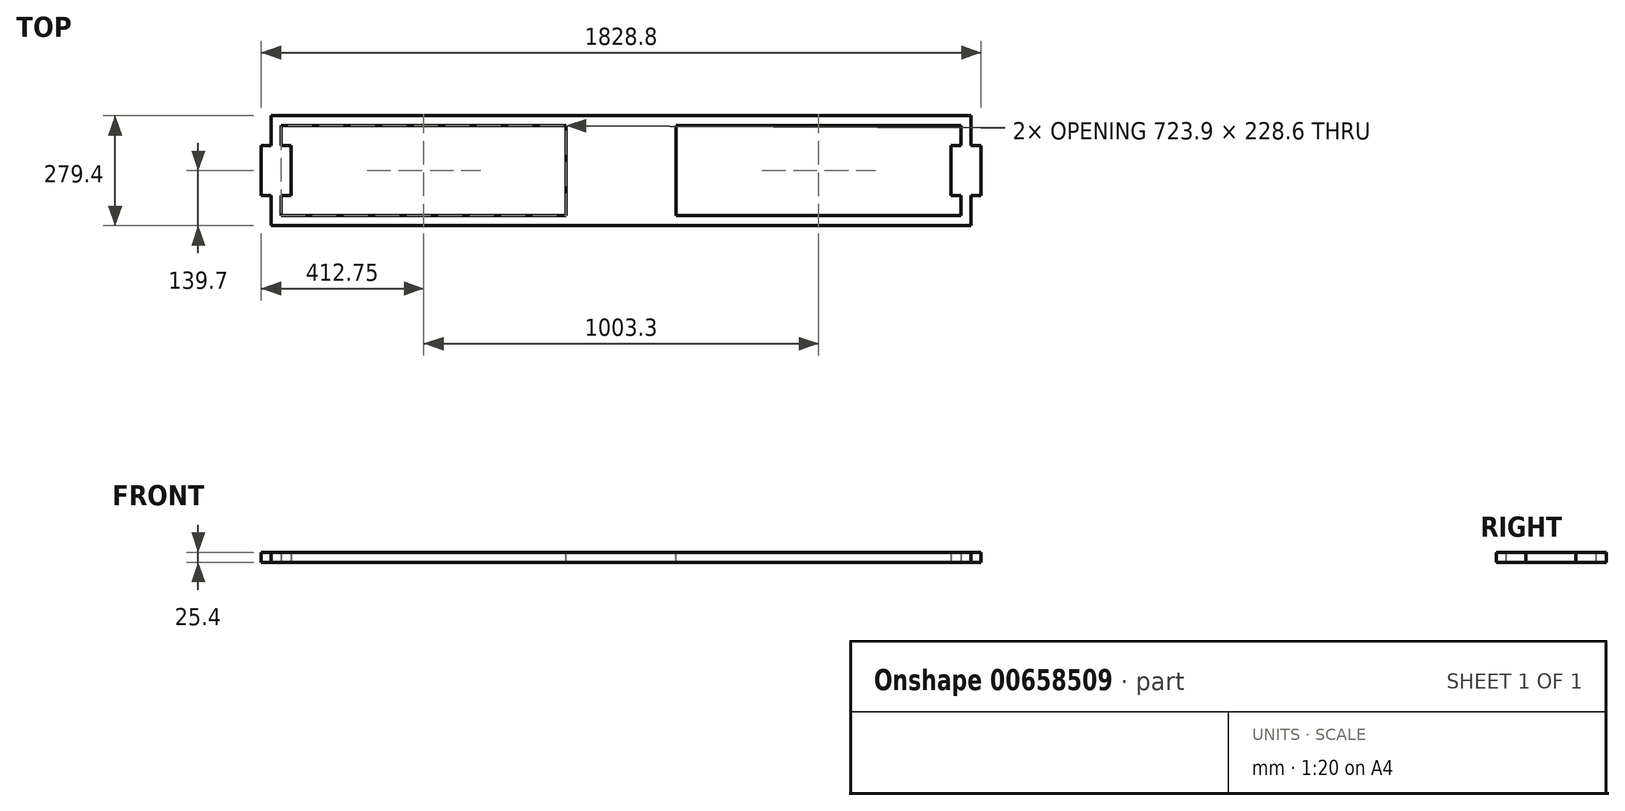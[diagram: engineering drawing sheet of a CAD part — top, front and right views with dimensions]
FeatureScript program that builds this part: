
annotation { "Feature Type Name" : "Feature", "Feature Type Description" : "" }
export const myFeature = defineFeature(function(context is Context, id is Id, definition is map)
    precondition{}
    {
        {
            var Q0;
            Q0=qCreatedBy(makeId("Top.planeOp"),FACE);
            var sketch = newSketch(context, id + "F0", { "sketchPlane" : qUnion([Q0])});
            skLineSegment(sketch, "E0.bottom", {"start": v(-889, 139.7) * mm, "end": v(889, 139.7) * mm});
            skLineSegment(sketch, "E0.top", {"start": v(-889, -139.7) * mm, "end": v(889, -139.7) * mm});
            skLineSegment(sketch, "E0.left", {"start": v(-889, 139.7) * mm, "end": v(-889, -139.7) * mm});
            skLineSegment(sketch, "E0.right", {"start": v(889, 139.7) * mm, "end": v(889, -139.7) * mm});
            skSolve(sketch);
        }
        {
            var Q0;
            Q0=makeQuery(id+"F0.imprint","IMPRINT",FACE,{"disambiguationData":[TD([[makeQuery(id+"F0.imprint","IMPRINT",EDGE,{"derivedFrom":sQuery(id+"F0.wireOp",EDGE,"E0.bottom")}),-1.0]])]});
            extrude(context, id + "F1", {"entities" : qUnion([Q0]), "depth" : 25.4 * mm, "offsetDistance" : 25.4 * mm});
        }
        {
            var Q0;
            Q0=makeQuery(id+"F1.opExtrude","CAP_FACE",FACE,{"disambiguationData":[OSD([sQuery(id+"F0.wireOp",EDGE,"E0.bottom"),sQuery(id+"F0.wireOp",EDGE,"E0.top"),sQuery(id+"F0.wireOp",EDGE,"E0.left"),sQuery(id+"F0.wireOp",EDGE,"E0.right")])],"isStart":false});
            var sketch = newSketch(context, id + "F2", { "sketchPlane" : qUnion([Q0])});
            skLineSegment(sketch, "E1.bottom", {"start": v(-863.6, 114.3) * mm, "end": v(863.6, 114.3) * mm});
            skLineSegment(sketch, "E1.top", {"start": v(-863.6, -114.3) * mm, "end": v(863.6, -114.3) * mm});
            skLineSegment(sketch, "E1.left", {"start": v(-863.6, 114.3) * mm, "end": v(-863.6, -114.3) * mm});
            skLineSegment(sketch, "E1.right", {"start": v(863.6, 114.3) * mm, "end": v(863.6, -114.3) * mm});
            skSolve(sketch);
        }
        {
            var Q0;
            Q0=makeQuery(id+"F2.imprint","IMPRINT",FACE,{"disambiguationData":[TD([[makeQuery(id+"F2.imprint","IMPRINT",EDGE,{"derivedFrom":sQuery(id+"F2.wireOp",EDGE,"E1.bottom")}),-1.0]])]});
            extrude(context, id + "F3", {"entities" : qUnion([Q0]), "operationType" : NewBodyOperationType.REMOVE, "endBound" : BoundingType.THROUGH_ALL, "oppositeDirection" : true, "depth" : 25.4 * mm, "offsetDistance" : 25.4 * mm});
        }
        {
            var Q0;
            Q0=qCreatedBy(makeId("Top.planeOp"),FACE);
            var sketch = newSketch(context, id + "F4", { "sketchPlane" : qUnion([Q0])});
            skLineSegment(sketch, "E2.bottom", {"start": v(-139.7, 139.7) * mm, "end": v(139.7, 139.7) * mm});
            skLineSegment(sketch, "E2.top", {"start": v(-139.7, -139.7) * mm, "end": v(139.7, -139.7) * mm});
            skLineSegment(sketch, "E2.left", {"start": v(-139.7, 139.7) * mm, "end": v(-139.7, -139.7) * mm});
            skLineSegment(sketch, "E2.right", {"start": v(139.7, 139.7) * mm, "end": v(139.7, -139.7) * mm});
            skSolve(sketch);
        }
        {
            var Q0;
            Q0=qSketchRegion(id+"F4",true);
            extrude(context, id + "F5", {"entities" : qUnion([Q0]), "operationType" : NewBodyOperationType.ADD, "depth" : 25.4 * mm, "offsetDistance" : 25.4 * mm});
        }
        {
            var Q0;
            Q0=makeQuery(id+"F1.opExtrude","SWEPT_FACE",FACE,{"disambiguationData":[OSD([sQuery(id+"F0.wireOp",EDGE,"E0.left")])]});
            var sketch = newSketch(context, id + "F6", { "sketchPlane" : qUnion([Q0])});
            skLineSegment(sketch, "E3.bottom", {"start": v(-63.5, 0) * mm, "end": v(63.5, 0) * mm});
            skLineSegment(sketch, "E3.top", {"start": v(-63.5, 25.4) * mm, "end": v(63.5, 25.4) * mm});
            skLineSegment(sketch, "E3.left", {"start": v(-63.5, 0) * mm, "end": v(-63.5, 25.4) * mm});
            skLineSegment(sketch, "E3.right", {"start": v(63.5, 0) * mm, "end": v(63.5, 25.4) * mm});
            skSolve(sketch);
        }
        {
            var Q0;
            Q0=makeQuery(id+"F6.imprint","IMPRINT",FACE,{"disambiguationData":[TD([[makeQuery(id+"F6.imprint","IMPRINT",EDGE,{"derivedFrom":sQuery(id+"F6.wireOp",EDGE,"E3.bottom")}),1.0]])]});
            extrude(context, id + "F7", {"entities" : qUnion([Q0]), "operationType" : NewBodyOperationType.ADD, "depth" : 25.4 * mm, "offsetDistance" : 25.4 * mm});
        }
        {
            var Q0;
            Q0=makeQuery(id+"F3.boolean.opBoolean","COPY",FACE,{"derivedFrom":makeQuery(id+"F3.opExtrude","SWEPT_FACE",FACE,{"disambiguationData":[OSD([sQuery(id+"F2.wireOp",EDGE,"E1.left")])]})});
            var sketch = newSketch(context, id + "F8", { "sketchPlane" : qUnion([Q0])});
            skLineSegment(sketch, "E4.bottom", {"start": v(-63.5, 25.4) * mm, "end": v(63.5, 25.4) * mm});
            skLineSegment(sketch, "E4.top", {"start": v(-63.5, 0) * mm, "end": v(63.5, 0) * mm});
            skLineSegment(sketch, "E4.left", {"start": v(-63.5, 25.4) * mm, "end": v(-63.5, 0) * mm});
            skLineSegment(sketch, "E4.right", {"start": v(63.5, 25.4) * mm, "end": v(63.5, 0) * mm});
            skSolve(sketch);
        }
        {
            var Q0;
            Q0=makeQuery(id+"F8.imprint","IMPRINT",FACE,{"disambiguationData":[TD([[makeQuery(id+"F8.imprint","IMPRINT",EDGE,{"derivedFrom":sQuery(id+"F8.wireOp",EDGE,"E4.bottom")}),1.0]])]});
            extrude(context, id + "F9", {"entities" : qUnion([Q0]), "operationType" : NewBodyOperationType.ADD, "depth" : 25.4 * mm, "offsetDistance" : 25.4 * mm});
        }
        {
            var Q0;
            Q0=makeQuery(id+"F1.opExtrude","SWEPT_FACE",FACE,{"disambiguationData":[OSD([sQuery(id+"F0.wireOp",EDGE,"E0.right")])]});
            var sketch = newSketch(context, id + "F10", { "sketchPlane" : qUnion([Q0])});
            skLineSegment(sketch, "E5.bottom", {"start": v(-63.5, 0) * mm, "end": v(63.5, 0) * mm});
            skLineSegment(sketch, "E5.top", {"start": v(-63.5, 25.4) * mm, "end": v(63.5, 25.4) * mm});
            skLineSegment(sketch, "E5.left", {"start": v(-63.5, 0) * mm, "end": v(-63.5, 25.4) * mm});
            skLineSegment(sketch, "E5.right", {"start": v(63.5, 0) * mm, "end": v(63.5, 25.4) * mm});
            skSolve(sketch);
        }
        {
            var Q0;
            Q0=makeQuery(id+"F10.imprint","IMPRINT",FACE,{"disambiguationData":[TD([[makeQuery(id+"F10.imprint","IMPRINT",EDGE,{"derivedFrom":sQuery(id+"F10.wireOp",EDGE,"E5.bottom")}),-1.0]])]});
            extrude(context, id + "F11", {"entities" : qUnion([Q0]), "operationType" : NewBodyOperationType.ADD, "depth" : 25.4 * mm, "offsetDistance" : 25.4 * mm});
        }
        {
            var Q0;
            Q0=makeQuery(id+"F3.boolean.opBoolean","COPY",FACE,{"derivedFrom":makeQuery(id+"F3.opExtrude","SWEPT_FACE",FACE,{"disambiguationData":[OSD([sQuery(id+"F2.wireOp",EDGE,"E1.right")])]})});
            var sketch = newSketch(context, id + "F12", { "sketchPlane" : qUnion([Q0])});
            skLineSegment(sketch, "E6.bottom", {"start": v(-63.5, 25.4) * mm, "end": v(63.5, 25.4) * mm});
            skLineSegment(sketch, "E6.top", {"start": v(-63.5, 0) * mm, "end": v(63.5, 0) * mm});
            skLineSegment(sketch, "E6.left", {"start": v(-63.5, 25.4) * mm, "end": v(-63.5, 0) * mm});
            skLineSegment(sketch, "E6.right", {"start": v(63.5, 25.4) * mm, "end": v(63.5, 0) * mm});
            skSolve(sketch);
        }
        {
            var Q0;
            Q0=makeQuery(id+"F12.imprint","IMPRINT",FACE,{"disambiguationData":[TD([[makeQuery(id+"F12.imprint","IMPRINT",EDGE,{"derivedFrom":sQuery(id+"F12.wireOp",EDGE,"E6.bottom")}),-1.0]])]});
            extrude(context, id + "F13", {"entities" : qUnion([Q0]), "operationType" : NewBodyOperationType.ADD, "depth" : 25.4 * mm, "offsetDistance" : 25.4 * mm});
        }
    });
